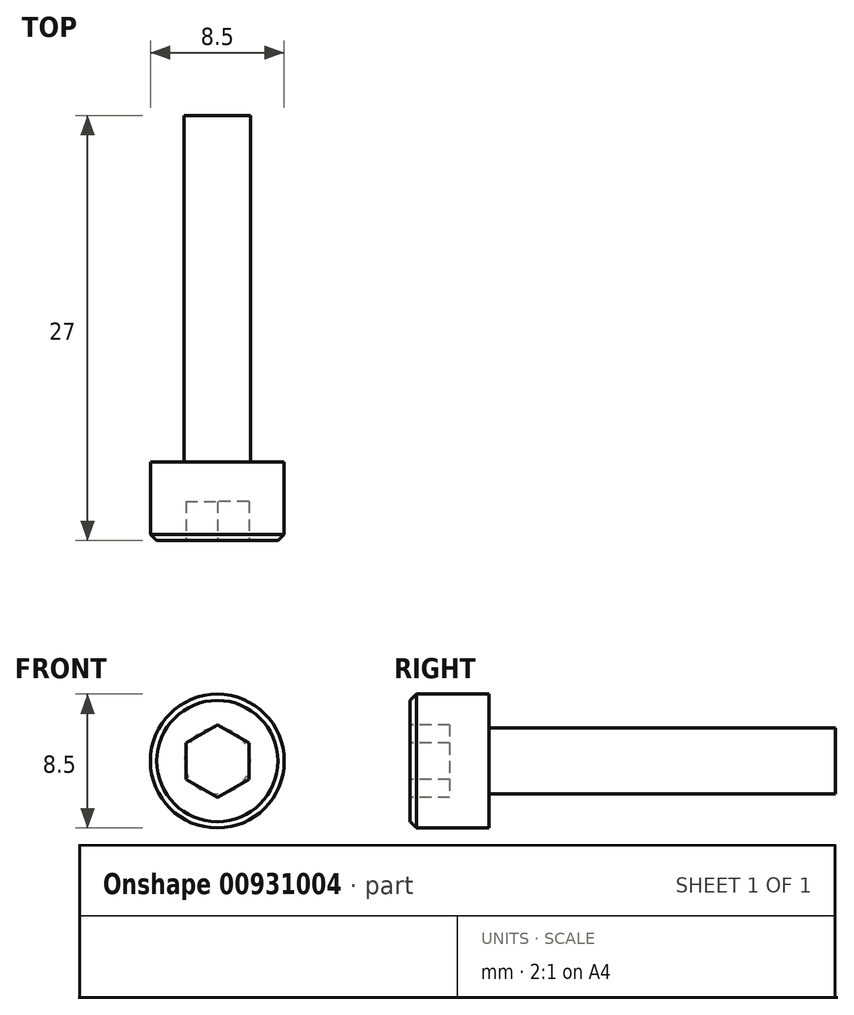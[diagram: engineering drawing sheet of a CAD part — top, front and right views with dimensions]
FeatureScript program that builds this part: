
annotation { "Feature Type Name" : "Feature", "Feature Type Description" : "" }
export const myFeature = defineFeature(function(context is Context, id is Id, definition is map)
    precondition{}
    {
        {
            var Q0;
            Q0=qCreatedBy(makeId("Front.planeOp"),FACE);
            var sketch = newSketch(context, id + "F0", { "sketchPlane" : qUnion([Q0])});
            skCircle(sketch, "E0", {"center": v(0, 0) * mm, "radius": 4.25 * mm});
            skSolve(sketch);
        }
        {
            var Q0;
            Q0=makeQuery(id+"F0.imprint","IMPRINT",FACE,{"disambiguationData":[TD([[makeQuery(id+"F0.imprint","IMPRINT",EDGE,{"derivedFrom":sQuery(id+"F0.wireOp",EDGE,"E0")}),1.0]])]});
            extrude(context, id + "F1", {"entities" : qUnion([Q0]), "depth" : 5 * mm, "offsetDistance" : 25 * mm});
        }
        {
            var Q0;
            Q0=makeQuery(id+"F1.opExtrude","CAP_FACE",FACE,{"disambiguationData":[OSD([sQuery(id+"F0.wireOp",EDGE,"E0")])],"isStart":true});
            var sketch = newSketch(context, id + "F2", { "sketchPlane" : qUnion([Q0])});
            skCircle(sketch, "E1", {"center": v(0, 0) * mm, "radius": 2.1 * mm});
            skSolve(sketch);
        }
        {
            var Q0;
            Q0=makeQuery(id+"F2.imprint","IMPRINT",FACE,{"disambiguationData":[TD([[makeQuery(id+"F2.imprint","IMPRINT",EDGE,{"derivedFrom":sQuery(id+"F2.wireOp",EDGE,"E1")}),1.0]])]});
            extrude(context, id + "F3", {"entities" : qUnion([Q0]), "operationType" : NewBodyOperationType.ADD, "depth" : 22 * mm, "offsetDistance" : 25 * mm});
        }
        {
            var Q0;
            Q0=makeQuery(id+"F1.opExtrude","CAP_FACE",FACE,{"disambiguationData":[OSD([sQuery(id+"F0.wireOp",EDGE,"E0")])],"isStart":false});
            var sketch = newSketch(context, id + "F4", { "sketchPlane" : qUnion([Q0])});
            skCircle(sketch, "E2.cCircle", {"center": v(0, 0) * mm, "radius": 2 * mm, "construction": true});
            skLineSegment(sketch, "E2.0", {"start": v(2, -1.15) * mm, "end": v(0, -2.3) * mm});
            skLineSegment(sketch, "E2.1", {"start": v(0, -2.3) * mm, "end": v(-2, -1.15) * mm});
            skLineSegment(sketch, "E2.2", {"start": v(-2, -1.15) * mm, "end": v(-2, 1.15) * mm});
            skLineSegment(sketch, "E2.3", {"start": v(-2, 1.15) * mm, "end": v(0, 2.3) * mm});
            skLineSegment(sketch, "E2.4", {"start": v(0, 2.3) * mm, "end": v(2, 1.15) * mm});
            skLineSegment(sketch, "E2.5", {"start": v(2, 1.15) * mm, "end": v(2, -1.15) * mm});
            skPoint(sketch, "E2.0.midPoint", {"position": v(1, -1.73) * mm});
            skLineSegment(sketch, "E3", {"start": v(0, 0) * mm, "end": v(4.25, 0) * mm, "construction": true});
            skSolve(sketch);
        }
        {
            var Q0;
            Q0=qSketchRegion(id+"F4",true);
            extrude(context, id + "F5", {"entities" : qUnion([Q0]), "operationType" : NewBodyOperationType.REMOVE, "oppositeDirection" : true, "depth" : 2.5 * mm, "offsetDistance" : 25 * mm});
        }
        {
            var Q0;
            Q0=makeQuery(id+"F1.opExtrude","CAP_EDGE",EDGE,{"disambiguationData":[OSD([sQuery(id+"F0.wireOp",EDGE,"E0")])],"isStart":false});
            chamfer(context, id + "F6", {"entities" : qUnion([Q0]), "width" : 0.4 * mm, "tangentPropagation" : true});
        }
    });
